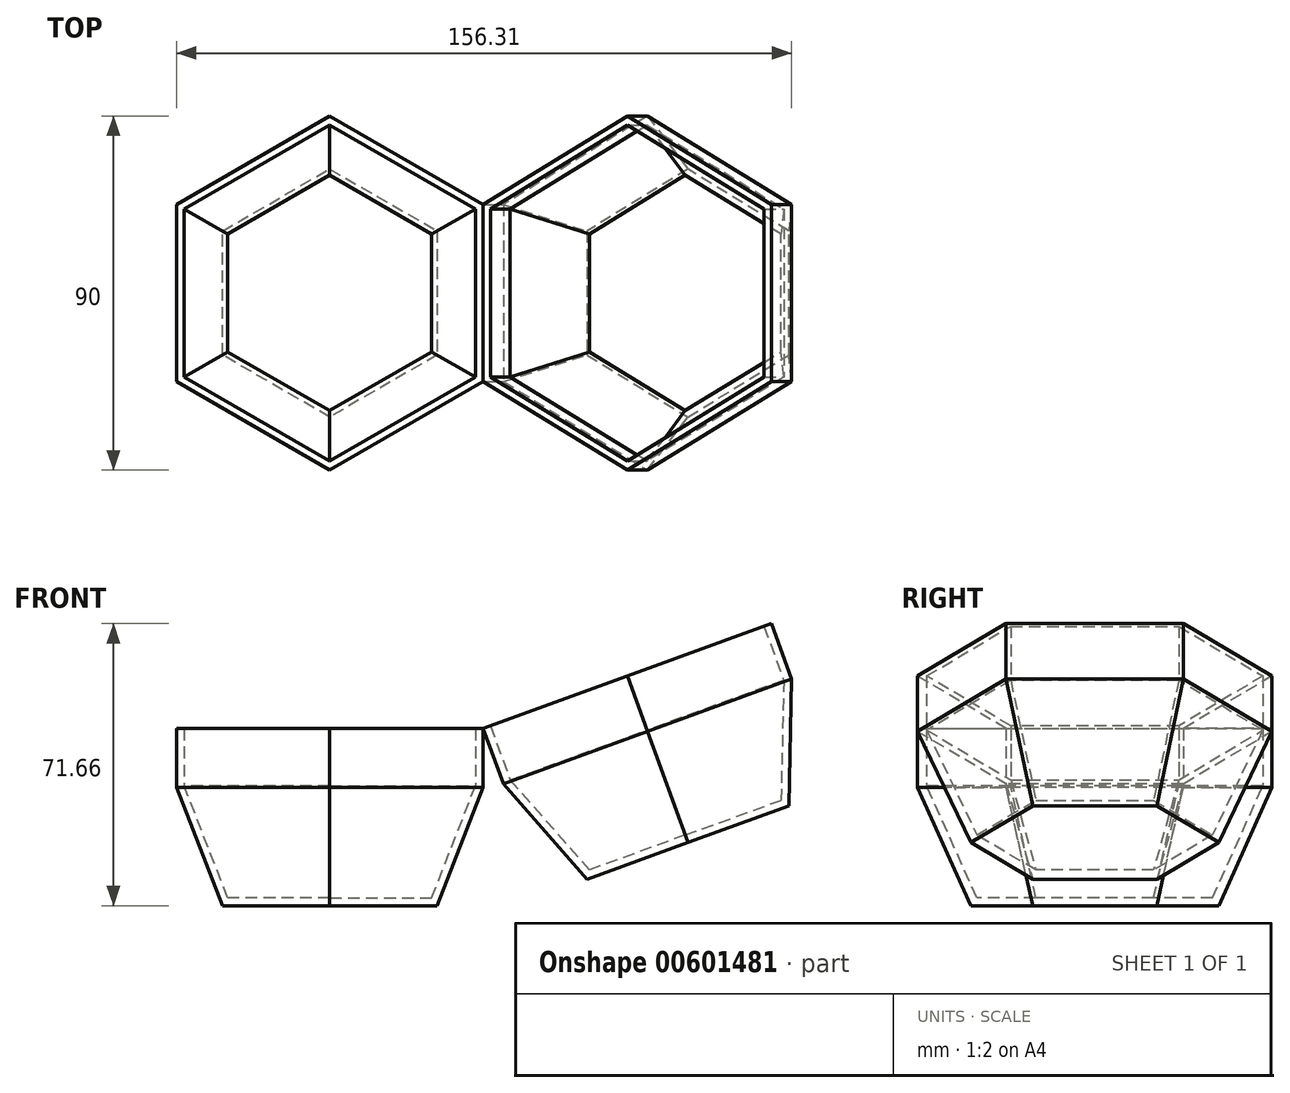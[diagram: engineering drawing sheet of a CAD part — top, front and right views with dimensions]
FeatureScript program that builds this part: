
annotation { "Feature Type Name" : "Feature", "Feature Type Description" : "" }
export const myFeature = defineFeature(function(context is Context, id is Id, definition is map)
    precondition{}
    {
        {
            var Q0;
            Q0=qCreatedBy(makeId("Top.planeOp"),FACE);
            var sketch = newSketch(context, id + "F0", { "sketchPlane" : qUnion([Q0])});
            skCircle(sketch, "E0.cCircle", {"center": v(0, 0) * mm, "radius": 31.5 * mm, "construction": true});
            skLineSegment(sketch, "E0.0", {"start": v(0, 31.5) * mm, "end": v(27.28, 15.75) * mm});
            skLineSegment(sketch, "E0.1", {"start": v(27.28, 15.75) * mm, "end": v(27.28, -15.75) * mm});
            skLineSegment(sketch, "E0.2", {"start": v(27.28, -15.75) * mm, "end": v(0, -31.5) * mm});
            skLineSegment(sketch, "E0.3", {"start": v(0, -31.5) * mm, "end": v(-27.28, -15.75) * mm});
            skLineSegment(sketch, "E0.4", {"start": v(-27.28, -15.75) * mm, "end": v(-27.28, 15.75) * mm});
            skLineSegment(sketch, "E0.5", {"start": v(-27.28, 15.75) * mm, "end": v(0, 31.5) * mm});
            skSolve(sketch);
        }
        {
            var Q0;
            Q0=makeQuery(id+"F0.imprint","IMPRINT",FACE,{"disambiguationData":[TD([[makeQuery(id+"F0.imprint","IMPRINT",EDGE,{"derivedFrom":sQuery(id+"F0.wireOp",EDGE,"E0.0")}),-1.0]])]});
            cPlane(context, id + "F1", {"entities" : qUnion([Q0]), "cplaneType" : CPlaneType.OFFSET, "offset" : 30 * mm, "width" : 150 * mm, "height" : 150 * mm});
        }
        {
            var Q0;
            Q0=qCreatedBy(id+"F1.planeOp",FACE);
            var sketch = newSketch(context, id + "F2", { "sketchPlane" : qUnion([Q0])});
            skCircle(sketch, "E1.cCircle", {"center": v(0, 0) * mm, "radius": 45 * mm, "construction": true});
            skLineSegment(sketch, "E1.0", {"start": v(0, 45) * mm, "end": v(38.97, 22.5) * mm});
            skLineSegment(sketch, "E1.1", {"start": v(38.97, 22.5) * mm, "end": v(38.97, -22.5) * mm});
            skLineSegment(sketch, "E1.2", {"start": v(38.97, -22.5) * mm, "end": v(0, -45) * mm});
            skLineSegment(sketch, "E1.3", {"start": v(0, -45) * mm, "end": v(-38.97, -22.5) * mm});
            skLineSegment(sketch, "E1.4", {"start": v(-38.97, -22.5) * mm, "end": v(-38.97, 22.5) * mm});
            skLineSegment(sketch, "E1.5", {"start": v(-38.97, 22.5) * mm, "end": v(0, 45) * mm});
            skSolve(sketch);
        }
        {
            var Q0;
            Q0=makeQuery(id+"F0.imprint","IMPRINT",FACE,{"disambiguationData":[TD([[makeQuery(id+"F0.imprint","IMPRINT",EDGE,{"derivedFrom":sQuery(id+"F0.wireOp",EDGE,"E0.0")}),-1.0]])]});
            var Q1;
            Q1=makeQuery(id+"F2.imprint","IMPRINT",FACE,{"disambiguationData":[TD([[makeQuery(id+"F2.imprint","IMPRINT",EDGE,{"derivedFrom":sQuery(id+"F2.wireOp",EDGE,"E1.0")}),-1.0]])]});
            loft(context, id + "F3", {"sheetProfilesArray" : [{ "sheetProfileEntities" : qUnion([Q0]) }, { "sheetProfileEntities" : qUnion([Q1]) }]});
        }
        {
            var Q0;
            Q0=makeQuery(id+"F3.opLoft","CAP_FACE",FACE,{"disambiguationData":[OSD([makeQuery(id+"F2.imprint","IMPRINT",FACE,{"disambiguationData":[TD([[makeQuery(id+"F2.imprint","IMPRINT",EDGE,{"derivedFrom":sQuery(id+"F2.wireOp",EDGE,"E1.0")}),-1.0]])]})])],"isStart":true});
            extrude(context, id + "F4", {"entities" : qUnion([Q0]), "operationType" : NewBodyOperationType.ADD, "depth" : 15 * mm, "offsetDistance" : 25 * mm});
        }
        {
            var Q0;
            Q0=makeQuery(id+"F4.opExtrude","CAP_FACE",FACE,{"disambiguationData":[OSD([makeQuery(id+"F2.imprint","IMPRINT",FACE,{"disambiguationData":[TD([[makeQuery(id+"F2.imprint","IMPRINT",EDGE,{"derivedFrom":sQuery(id+"F2.wireOp",EDGE,"E1.0")}),-1.0]])]})])],"isStart":false});
            shell(context, id + "F5", {"entities" : qUnion([Q0]), "thickness" : 2 * mm});
        }
        {
            var Q0;
            Q0=makeQuery(id+"F4.opExtrude","CAP_EDGE",EDGE,{"disambiguationData":[OSD([sQuery(id+"F2.wireOp",EDGE,"E1.0"),sQuery(id+"F2.wireOp",EDGE,"E1.1"),sQuery(id+"F2.wireOp",EDGE,"E1.2")])],"isStart":false});
            cPlane(context, id + "F6", {"entities" : qUnion([Q0]), "cplaneType" : CPlaneType.LINE_ANGLE, "offset" : 25 * mm, "angle" : 20 * degree, "width" : 150 * mm, "height" : 150 * mm});
        }
        {
            var Q0;
            Q0=qCreatedBy(id+"F6.planeOp",FACE);
            var sketch = newSketch(context, id + "F7", { "sketchPlane" : qUnion([Q0])});
            skLineSegment(sketch, "E2", {"start": v(0, 0) * mm, "end": v(201, 0) * mm, "construction": true});
            skCircle(sketch, "E3.cCircle", {"center": v(90.98, 0) * mm, "radius": 45 * mm, "construction": true});
            skLineSegment(sketch, "E3.0", {"start": v(90.98, 45) * mm, "end": v(129.95, 22.5) * mm});
            skLineSegment(sketch, "E3.1", {"start": v(129.95, 22.5) * mm, "end": v(129.95, -22.5) * mm});
            skLineSegment(sketch, "E3.2", {"start": v(129.95, -22.5) * mm, "end": v(90.98, -45) * mm});
            skLineSegment(sketch, "E3.3", {"start": v(90.98, -45) * mm, "end": v(52.01, -22.5) * mm});
            skLineSegment(sketch, "E3.4", {"start": v(52.01, -22.5) * mm, "end": v(52.01, 22.5) * mm});
            skLineSegment(sketch, "E3.5", {"start": v(52.01, 22.5) * mm, "end": v(90.98, 45) * mm});
            skSolve(sketch);
        }
        {
            var Q0;
            Q0=makeQuery(id+"F7.imprint","IMPRINT",FACE,{"disambiguationData":[TD([[makeQuery(id+"F7.imprint","IMPRINT",EDGE,{"derivedFrom":sQuery(id+"F7.wireOp",EDGE,"E3.0")}),-1.0]])]});
            cPlane(context, id + "F8", {"entities" : qUnion([Q0]), "cplaneType" : CPlaneType.OFFSET, "offset" : 15 * mm, "width" : 150 * mm, "height" : 150 * mm});
        }
        {
            var Q0;
            Q0=qCreatedBy(id+"F8.planeOp",FACE);
            var sketch = newSketch(context, id + "F9", { "sketchPlane" : qUnion([Q0])});
            skLineSegment(sketch, "E4", {"start": v(-1.2, 0) * mm, "end": v(199.82, 0) * mm, "construction": true});
            skCircle(sketch, "E5.cCircle", {"center": v(90.98, 0) * mm, "radius": 45 * mm, "construction": true});
            skLineSegment(sketch, "E5.0", {"start": v(90.98, 45) * mm, "end": v(129.95, 22.5) * mm});
            skLineSegment(sketch, "E5.1", {"start": v(129.95, 22.5) * mm, "end": v(129.95, -22.5) * mm});
            skLineSegment(sketch, "E5.2", {"start": v(129.95, -22.5) * mm, "end": v(90.98, -45) * mm});
            skLineSegment(sketch, "E5.3", {"start": v(90.98, -45) * mm, "end": v(52.01, -22.5) * mm});
            skLineSegment(sketch, "E5.4", {"start": v(52.01, -22.5) * mm, "end": v(52.01, 22.5) * mm});
            skLineSegment(sketch, "E5.5", {"start": v(52.01, 22.5) * mm, "end": v(90.98, 45) * mm});
            skSolve(sketch);
        }
        {
            var Q0;
            Q0=makeQuery(id+"F9.imprint","IMPRINT",FACE,{"disambiguationData":[TD([[makeQuery(id+"F9.imprint","IMPRINT",EDGE,{"derivedFrom":sQuery(id+"F9.wireOp",EDGE,"E5.0")}),-1.0]])]});
            cPlane(context, id + "F10", {"entities" : qUnion([Q0]), "cplaneType" : CPlaneType.OFFSET, "offset" : 30 * mm, "width" : 150 * mm, "height" : 150 * mm});
        }
        {
            var Q0;
            Q0=qCreatedBy(id+"F10.planeOp",FACE);
            var sketch = newSketch(context, id + "F11", { "sketchPlane" : qUnion([Q0])});
            skLineSegment(sketch, "E6", {"start": v(26.46, 0) * mm, "end": v(167.17, 0) * mm, "construction": true});
            skCircle(sketch, "E7.cCircle", {"center": v(90.98, 0) * mm, "radius": 31.5 * mm, "construction": true});
            skLineSegment(sketch, "E7.0", {"start": v(90.98, 31.5) * mm, "end": v(118.26, 15.75) * mm});
            skLineSegment(sketch, "E7.1", {"start": v(118.26, 15.75) * mm, "end": v(118.26, -15.75) * mm});
            skLineSegment(sketch, "E7.2", {"start": v(118.26, -15.75) * mm, "end": v(90.98, -31.5) * mm});
            skLineSegment(sketch, "E7.3", {"start": v(90.98, -31.5) * mm, "end": v(63.7, -15.75) * mm});
            skLineSegment(sketch, "E7.4", {"start": v(63.7, -15.75) * mm, "end": v(63.7, 15.75) * mm});
            skLineSegment(sketch, "E7.5", {"start": v(63.7, 15.75) * mm, "end": v(90.98, 31.5) * mm});
            skSolve(sketch);
        }
        {
            var Q0;
            Q0=makeQuery(id+"F7.imprint","IMPRINT",FACE,{"disambiguationData":[TD([[makeQuery(id+"F7.imprint","IMPRINT",EDGE,{"derivedFrom":sQuery(id+"F7.wireOp",EDGE,"E3.0")}),-1.0]])]});
            var Q1;
            Q1=makeQuery(id+"F9.imprint","IMPRINT",FACE,{"disambiguationData":[TD([[makeQuery(id+"F9.imprint","IMPRINT",EDGE,{"derivedFrom":sQuery(id+"F9.wireOp",EDGE,"E5.0")}),-1.0]])]});
            loft(context, id + "F12", {"sheetProfilesArray" : [{ "sheetProfileEntities" : qUnion([Q0]) }, { "sheetProfileEntities" : qUnion([Q1]) }]});
        }
        {
            var Q1;
            Q1=makeQuery(id+"F12.opLoft","CAP_FACE",FACE,{"disambiguationData":[OSD([makeQuery(id+"F9.imprint","IMPRINT",FACE,{"disambiguationData":[TD([[makeQuery(id+"F9.imprint","IMPRINT",EDGE,{"derivedFrom":sQuery(id+"F9.wireOp",EDGE,"E5.0")}),-1.0]])]})])],"isStart":true});
            var Q2;
            Q2=makeQuery(id+"F11.imprint","IMPRINT",FACE,{"disambiguationData":[TD([[makeQuery(id+"F11.imprint","IMPRINT",EDGE,{"derivedFrom":sQuery(id+"F11.wireOp",EDGE,"E7.0")}),-1.0]])]});
            loft(context, id + "F13", {"operationType" : NewBodyOperationType.ADD, "sheetProfilesArray" : [{ "sheetProfileEntities" : qUnion([Q1]) }, { "sheetProfileEntities" : qUnion([Q2]) }]});
        }
        {
            var Q0;
            Q0=makeQuery(id+"F12.opLoft","CAP_FACE",FACE,{"disambiguationData":[OSD([makeQuery(id+"F7.imprint","IMPRINT",FACE,{"disambiguationData":[TD([[makeQuery(id+"F7.imprint","IMPRINT",EDGE,{"derivedFrom":sQuery(id+"F7.wireOp",EDGE,"E3.0")}),-1.0]])]})])],"isStart":true});
            shell(context, id + "F14", {"entities" : qUnion([Q0]), "thickness" : 2 * mm});
        }
    });
